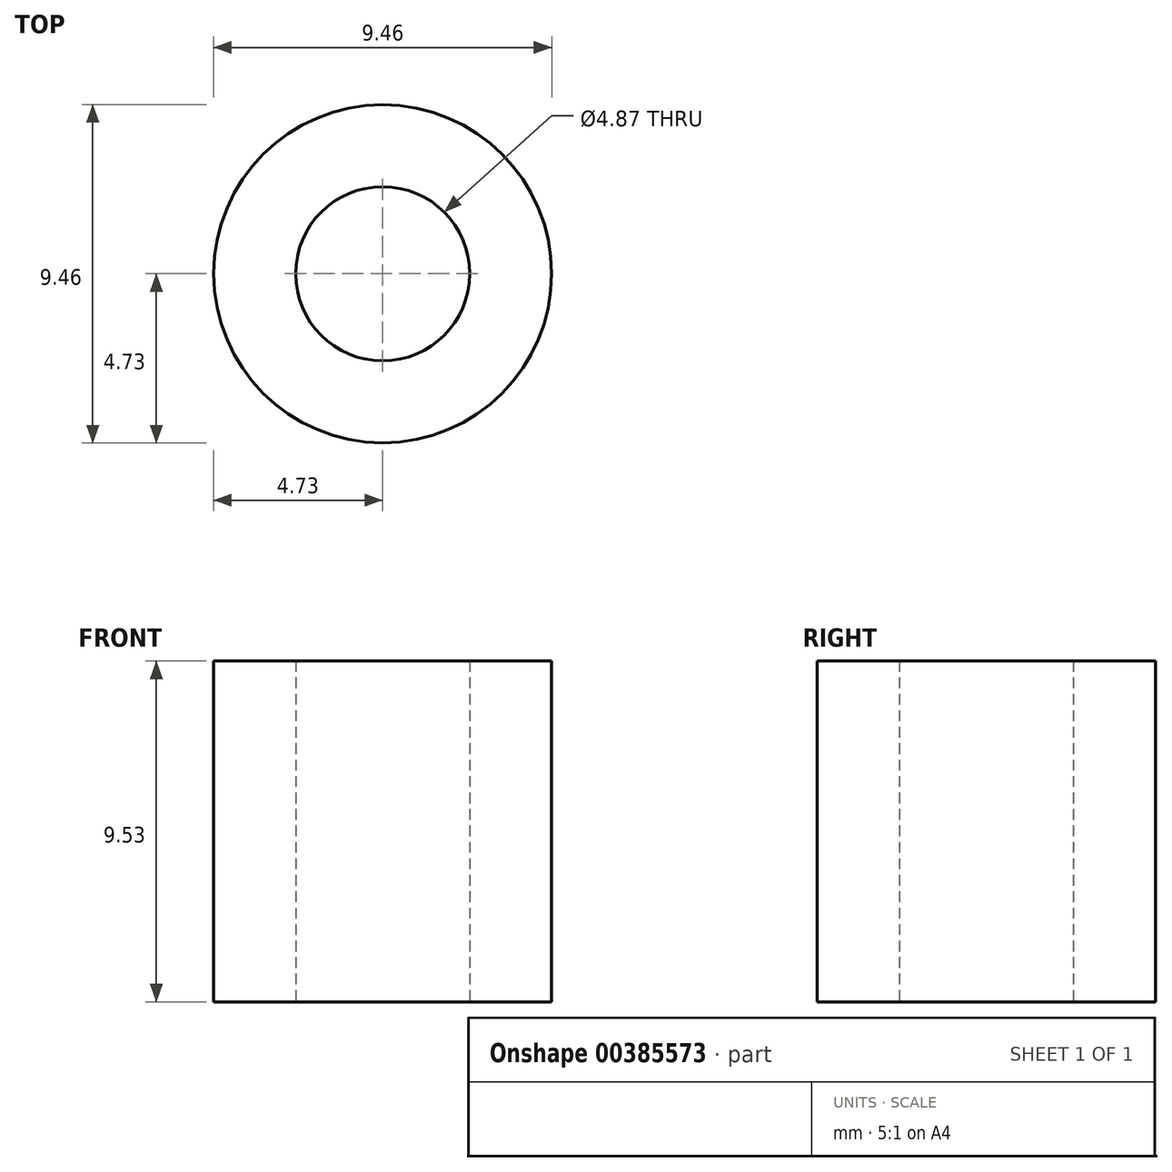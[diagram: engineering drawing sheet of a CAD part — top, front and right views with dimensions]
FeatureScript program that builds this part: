
annotation { "Feature Type Name" : "Feature", "Feature Type Description" : "" }
export const myFeature = defineFeature(function(context is Context, id is Id, definition is map)
    precondition{}
    {
        {
            var Q0;
            Q0=qCreatedBy(makeId("Top.planeOp"),FACE);
            var sketch = newSketch(context, id + "F0", { "sketchPlane" : qUnion([Q0])});
            skCircle(sketch, "E0", {"center": v(0, 0) * mm, "radius": 4.72 * mm});
            skCircle(sketch, "E1", {"center": v(0, 0) * mm, "radius": 2.44 * mm});
            skSolve(sketch);
        }
        {
            var Q0;
            Q0 = qSketchRegion(id + "F0", true);
            extrude(context, id + "F1", {"entities" : qUnion([Q0]), "depth" : 9.53 * mm});
        }
    });
